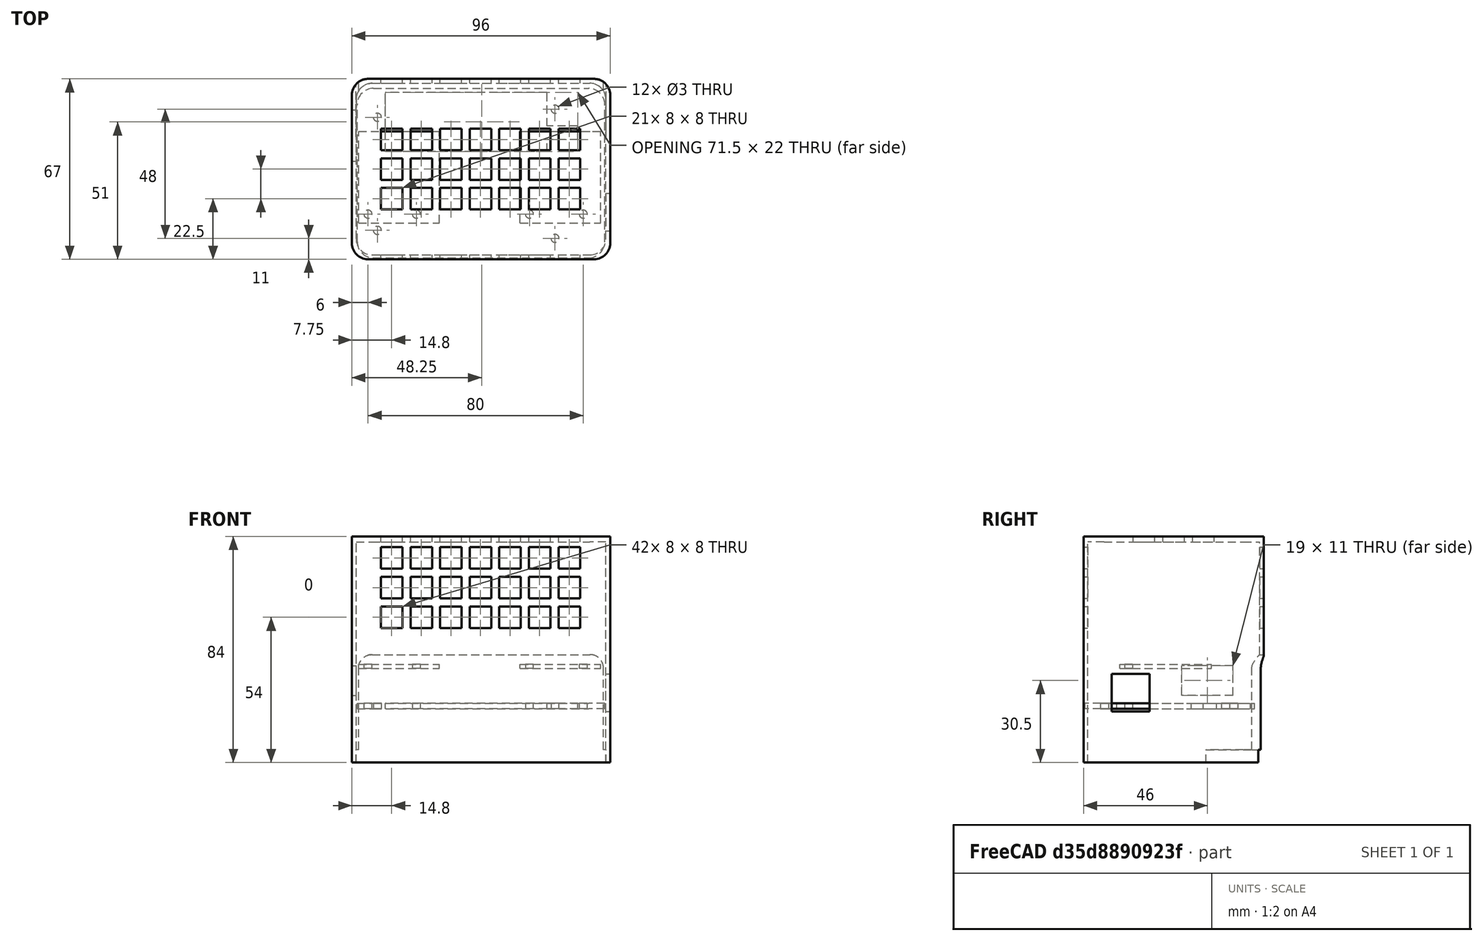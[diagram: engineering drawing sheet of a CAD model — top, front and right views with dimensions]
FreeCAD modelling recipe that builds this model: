
FCSTD DOCUMENT  (FreeCAD 0.18.4R)
Label: BBBCase1
License: CC-BY 3.0
LicenseURL: http://creativecommons.org/licenses/by/3.0/
objects: Part::Box×58, Part::Cylinder×20, Part::MultiFuse×17, Part::Cut×15, Part::Fillet×6, Part::Feature×2, Mesh::Feature×1
note: 118 computed .brp shape members not serialized (recipe doc carries the construction recipe); baked Part::Feature solids carry a one-line shape summary decoded from their .brp

FEATURE [Part::Cylinder] Cylinder
  Angle = 360
  AttacherType = Attacher::AttachEngine3D
  Height = 20
  Placement = pos=(5.5,9.25,0) rot=(0,0,1;0rad)
  Radius = 1.5
FEATURE [Part::Cylinder] Cylinder001
  Angle = 360
  AttacherType = Attacher::AttachEngine3D
  Height = 20
  Placement = pos=(5.5,51.25,0) rot=(0,0,1;0rad)
  Radius = 1.5
FEATURE [Part::Cylinder] Cylinder002
  Angle = 360
  AttacherType = Attacher::AttachEngine3D
  Height = 20
  Placement = pos=(71.5,54.25,0) rot=(0,0,1;0rad)
  Radius = 1.5
FEATURE [Part::Cylinder] Cylinder003
  Angle = 360
  AttacherType = Attacher::AttachEngine3D
  Height = 20
  Placement = pos=(71.5,6.25,0) rot=(0,0,1;0rad)
  Radius = 1.5
FEATURE [Part::Box] Box001  label="base-cube001"
  AttacherType = Attacher::AttachEngine3D
  Height = 2
  Length = 92
  Placement = pos=(-2,-1,0) rot=(0,0,1;0rad)
  Width = 63
FEATURE [Part::Fillet] Fillet
  Base = -> Box001
  Edges = 4 edges r=6: [Edge1,Edge3,Edge5,Edge7]
FEATURE [Part::Cylinder] Cylinder004
  Angle = 360
  AttacherType = Attacher::AttachEngine3D
  Height = 20
  Placement = pos=(5.5,9.25,0) rot=(0,0,1;0rad)
  Radius = 3
FEATURE [Part::Cylinder] Cylinder005
  Angle = 360
  AttacherType = Attacher::AttachEngine3D
  Height = 20
  Placement = pos=(5.5,51.25,0) rot=(0,0,1;0rad)
  Radius = 3
FEATURE [Part::Cylinder] Cylinder006
  Angle = 360
  AttacherType = Attacher::AttachEngine3D
  Height = 20
  Placement = pos=(71.5,54.25,0) rot=(0,0,1;0rad)
  Radius = 3
FEATURE [Part::Cylinder] Cylinder007
  Angle = 360
  AttacherType = Attacher::AttachEngine3D
  Height = 20
  Placement = pos=(71.5,6.25,0) rot=(0,0,1;0rad)
  Radius = 3
FEATURE [Part::MultiFuse] Fusion
  Shapes = -> [Cylinder007,Cylinder006,Cylinder005,Cylinder004,Fillet]
FEATURE [Part::MultiFuse] Fusion001
  Shapes = -> [Cylinder003,Cylinder002,Cylinder001,Cylinder]
FEATURE [Part::Cut] Cut
  Base = -> Fusion
  Tool = -> Fusion001
FEATURE [Part::Box] Box002  label="Cube"
  AttacherType = Attacher::AttachEngine3D
  Height = 10
  Length = 56.5
  Placement = pos=(11,1,0) rot=(0,0,1;0rad)
  Width = 59
FEATURE [Part::Cut] Cut001
  Base = -> Cut
  Tool = -> Box002
FEATURE [Part::Box] Box003  label="base-cube002"
  AttacherType = Attacher::AttachEngine3D
  Height = 2
  Length = 92
  Placement = pos=(-2,-1,0) rot=(0,0,1;0rad)
  Width = 63
FEATURE [Part::Fillet] Fillet001
  Base = -> Box003
  Edges = 4 edges r=6: [Edge1,Edge3,Edge5,Edge7]
  Placement = pos=(0,0,26) rot=(0,0,1;0rad)
FEATURE [Part::Cylinder] Cylinder008
  Angle = 360
  AttacherType = Attacher::AttachEngine3D
  Height = 20
  Placement = pos=(71.5,6.25,20) rot=(0,0,1;0rad)
  Radius = 1.5
FEATURE [Part::Cylinder] Cylinder009
  Angle = 360
  AttacherType = Attacher::AttachEngine3D
  Height = 20
  Placement = pos=(5.5,9.25,20) rot=(0,0,1;0rad)
  Radius = 1.5
FEATURE [Part::Cylinder] Cylinder010
  Angle = 360
  AttacherType = Attacher::AttachEngine3D
  Height = 20
  Placement = pos=(5.5,51.25,20) rot=(0,0,1;0rad)
  Radius = 1.5
FEATURE [Part::Cylinder] Cylinder011
  Angle = 360
  AttacherType = Attacher::AttachEngine3D
  Height = 20
  Placement = pos=(71.5,54.25,20) rot=(0,0,1;0rad)
  Radius = 1.5
FEATURE [Part::MultiFuse] Fusion002
  Shapes = -> [Cylinder008,Cylinder009,Cylinder010,Cylinder011]
FEATURE [Part::Cut] Cut002
  Base = -> Fillet001
  Tool = -> Fusion002
FEATURE [Part::Box] Box005  label="Cube002"
  AttacherType = Attacher::AttachEngine3D
  Height = 1.5
  Length = 30
  Placement = pos=(58.5,12,35) rot=(0,0,1;0rad)
  Width = 34
FEATURE [Part::Cylinder] Cylinder012
  Angle = 360
  AttacherType = Attacher::AttachEngine3D
  Height = 20
  Placement = pos=(2,15.25,20) rot=(0,0,1;0rad)
  Radius = 1.5
FEATURE [Part::Cylinder] Cylinder013
  Angle = 360
  AttacherType = Attacher::AttachEngine3D
  Height = 20
  Placement = pos=(20,15.25,20) rot=(0,0,1;0rad)
  Radius = 1.5
FEATURE [Part::Cylinder] Cylinder014
  Angle = 360
  AttacherType = Attacher::AttachEngine3D
  Height = 20
  Placement = pos=(82,15.25,20) rot=(0,0,1;0rad)
  Radius = 1.5
FEATURE [Part::Cylinder] Cylinder015
  Angle = 360
  AttacherType = Attacher::AttachEngine3D
  Height = 20
  Placement = pos=(62,15.25,20) rot=(0,0,1;0rad)
  Radius = 1.5
FEATURE [Part::Box] Box006  label="Cube003"
  AttacherType = Attacher::AttachEngine3D
  Height = 1.5
  Length = 30
  Placement = pos=(-1.5,12,35) rot=(0,0,1;0rad)
  Width = 34
FEATURE [Part::MultiFuse] Fusion003
  Shapes = -> [Cylinder015,Cylinder014,Cylinder013,Cylinder012]
FEATURE [Part::Cut] Cut003  label="PRE-GPS-BASE"
  Base = -> Cut002
  Tool = -> Fusion003
FEATURE [Part::Cylinder] Cylinder016
  Angle = 360
  AttacherType = Attacher::AttachEngine3D
  Height = 20
  Placement = pos=(2,15.25,20) rot=(0,0,1;0rad)
  Radius = 1.5
FEATURE [Part::Cylinder] Cylinder017
  Angle = 360
  AttacherType = Attacher::AttachEngine3D
  Height = 20
  Placement = pos=(20,15.25,20) rot=(0,0,1;0rad)
  Radius = 1.5
FEATURE [Part::Cylinder] Cylinder018
  Angle = 360
  AttacherType = Attacher::AttachEngine3D
  Height = 20
  Placement = pos=(82,15.25,20) rot=(0,0,1;0rad)
  Radius = 1.5
FEATURE [Part::Cylinder] Cylinder019
  Angle = 360
  AttacherType = Attacher::AttachEngine3D
  Height = 20
  Placement = pos=(62,15.25,20) rot=(0,0,1;0rad)
  Radius = 1.5
FEATURE [Part::MultiFuse] Fusion004
  Shapes = -> [Cylinder017,Cylinder016]
FEATURE [Part::MultiFuse] Fusion005
  Shapes = -> [Cylinder019,Cylinder018]
FEATURE [Part::Cut] Cut004  label="SUP-GPS-B"
  Base = -> Box006
  Tool = -> Fusion004
FEATURE [Part::Cut] Cut005  label="SUP-GPS-A"
  Base = -> Box005
  Tool = -> Fusion005
FEATURE [Part::Box] Box007  label="Cube004"
  AttacherType = Attacher::AttachEngine3D
  Height = 10
  Length = 87
  Placement = pos=(0.5,20,0) rot=(0,0,1;0rad)
  Width = 20
FEATURE [Part::Cut] Cut006  label="BOTTON-BASE"
  Base = -> Cut001
  Tool = -> Box007
FEATURE [Part::Box] Box008  label="Cube005"
  AttacherType = Attacher::AttachEngine3D
  Height = 10
  Length = 60
  Placement = pos=(8.5,38.5,20) rot=(0,0,1;0rad)
  Width = 22
FEATURE [Part::Cut] Cut007  label="pre-MIDDLE-BASE"
  Base = -> Cut003
  Tool = -> Box008
FEATURE [Part::Box] Box009  label="Cube006"
  AttacherType = Attacher::AttachEngine3D
  Height = 10
  Length = 12
  Placement = pos=(68,43,20) rot=(0,0,1;0rad)
  Width = 5
FEATURE [Part::Cut] Cut008  label="MIDDLE-BASE"
  Base = -> Cut007
  Placement = pos=(0,0,-6) rot=(0,0,1;0rad)
  Tool = -> Box009
FEATURE [Mesh::Feature] lcd_housing
  Placement = pos=(-1,62,-0.01) rot=(0,0,1;0rad)
FEATURE [Part::Box] Box010  label="base-cube003"
  AttacherType = Attacher::AttachEngine3D
  Height = 4.5
  Length = 92
  Placement = pos=(-2,47,0) rot=(0,0,1;0rad)
  Width = 52
FEATURE [Part::Fillet] Fillet002
  Base = -> Box010
  Edges = 2 edges r=5: [Edge3,Edge7]
FEATURE [Part::Feature] lcd_housing001
  shape: bbox 90 x 37 x 39.75 mm, 3808 faces, 0 solids (baked)
FEATURE [Part::Feature] lcd_housing001_solid  label="lcd_housing001 (Solid)"
  shape: bbox 90 x 37 x 39.75 mm, 3808 faces (baked)
FEATURE [Part::MultiFuse] Fusion006
  Shapes = -> [lcd_housing001_solid,Fillet002,Cut006]
FEATURE [Part::Box] Box011  label="Cube007"
  AttacherType = Attacher::AttachEngine3D
  Height = 10
  Length = 82
  Placement = pos=(3,59,-1) rot=(0,0,1;0rad)
  Width = 36
FEATURE [Part::Cut] Cut009  label="bottom-base"
  Base = -> Fusion006
  Tool = -> Box011
FEATURE [Part::Box] Box012  label="base-cube004"
  AttacherType = Attacher::AttachEngine3D
  Height = 82
  Length = 92.8
  Placement = pos=(-2,-1,0) rot=(0,0,1;0rad)
  Width = 63.8
FEATURE [Part::Fillet] Fillet003
  Base = -> Box012
  Edges = 4 edges r=6: [Edge1,Edge3,Edge5,Edge7]
  Placement = pos=(1.6,1.6,26) rot=(0,0,1;0rad)
FEATURE [Part::Box] Box013  label="base-cube005"
  AttacherType = Attacher::AttachEngine3D
  Height = 84
  Length = 96
  Placement = pos=(-2,-1,0) rot=(0,0,1;0rad)
  Width = 67
FEATURE [Part::Fillet] Fillet004
  Base = -> Box013
  Edges = 4 edges r=6: [Edge1,Edge3,Edge5,Edge7]
  Placement = pos=(0,0,26) rot=(0,0,1;0rad)
FEATURE [Part::Cut] Cut009002001002
  Base = -> Fillet004
  Placement = pos=(-2,-0.5,-26) rot=(0,0,1;0rad)
  Tool = -> Fillet003
FEATURE [Part::Box] Box  label="Cube008"
  AttacherType = Attacher::AttachEngine3D
  Height = 35.5
  Length = 91
  Placement = pos=(-1.5,53,4.6) rot=(0,0,1;0rad)
  Width = 10
FEATURE [Part::Fillet] Fillet005
  Base = -> Box
  Edges = 2 edges r=5: [Edge2,Edge6]
  Placement = pos=(0,5,0) rot=(0,0,1;0rad)
FEATURE [Part::Box] Box014  label="Cube009"
  AttacherType = Attacher::AttachEngine3D
  Height = 4.8
  Length = 93
  Placement = pos=(-2.5,44,0) rot=(0,0,1;0rad)
  Width = 64
FEATURE [Part::MultiFuse] Fusion007
  Shapes = -> [Box014,Fillet005]
FEATURE [Part::Cut] Cut009002001003
  Base = -> Cut009002001002
  Tool = -> Fusion007
FEATURE [Part::Box] Box015  label="Cube010"
  AttacherType = Attacher::AttachEngine3D
  Height = 8
  Length = 8
  Placement = pos=(5,-9,72) rot=(0,0,1;0rad)
  Width = 89
FEATURE [Part::Box] Box016  label="Cube011"
  AttacherType = Attacher::AttachEngine3D
  Height = 8
  Length = 8
  Placement = pos=(16,-9,72) rot=(0,0,1;0rad)
  Width = 89
FEATURE [Part::Box] Box017  label="Cube012"
  AttacherType = Attacher::AttachEngine3D
  Height = 8
  Length = 8
  Placement = pos=(27,-9,72) rot=(0,0,1;0rad)
  Width = 89
FEATURE [Part::Box] Box018  label="Cube013"
  AttacherType = Attacher::AttachEngine3D
  Height = 8
  Length = 8
  Placement = pos=(38,-9,72) rot=(0,0,1;0rad)
  Width = 89
FEATURE [Part::Box] Box019  label="Cube014"
  AttacherType = Attacher::AttachEngine3D
  Height = 8
  Length = 8
  Placement = pos=(49,-9,72) rot=(0,0,1;0rad)
  Width = 89
FEATURE [Part::Box] Box020  label="Cube015"
  AttacherType = Attacher::AttachEngine3D
  Height = 8
  Length = 8
  Placement = pos=(60,-9,72) rot=(0,0,1;0rad)
  Width = 89
FEATURE [Part::Box] Box021  label="Cube016"
  AttacherType = Attacher::AttachEngine3D
  Height = 8
  Length = 8
  Placement = pos=(71,-9,72) rot=(0,0,1;0rad)
  Width = 89
FEATURE [Part::MultiFuse] Fusion008
  Placement = pos=(1.8,0,0) rot=(0,0,1;0rad)
  Shapes = -> [Box021,Box015,Box016,Box017,Box018,Box019,Box020]
FEATURE [Part::Box] Box022  label="Cube017"
  AttacherType = Attacher::AttachEngine3D
  Height = 8
  Length = 8
  Placement = pos=(5,-9,72) rot=(0,0,1;0rad)
  Width = 89
FEATURE [Part::Box] Box023  label="Cube018"
  AttacherType = Attacher::AttachEngine3D
  Height = 8
  Length = 8
  Placement = pos=(16,-9,72) rot=(0,0,1;0rad)
  Width = 89
FEATURE [Part::Box] Box024  label="Cube019"
  AttacherType = Attacher::AttachEngine3D
  Height = 8
  Length = 8
  Placement = pos=(27,-9,72) rot=(0,0,1;0rad)
  Width = 89
FEATURE [Part::Box] Box025  label="Cube020"
  AttacherType = Attacher::AttachEngine3D
  Height = 8
  Length = 8
  Placement = pos=(38,-9,72) rot=(0,0,1;0rad)
  Width = 89
FEATURE [Part::Box] Box026  label="Cube021"
  AttacherType = Attacher::AttachEngine3D
  Height = 8
  Length = 8
  Placement = pos=(49,-9,72) rot=(0,0,1;0rad)
  Width = 89
FEATURE [Part::Box] Box027  label="Cube022"
  AttacherType = Attacher::AttachEngine3D
  Height = 8
  Length = 8
  Placement = pos=(60,-9,72) rot=(0,0,1;0rad)
  Width = 89
FEATURE [Part::Box] Box028  label="Cube023"
  AttacherType = Attacher::AttachEngine3D
  Height = 8
  Length = 8
  Placement = pos=(71,-9,72) rot=(0,0,1;0rad)
  Width = 89
FEATURE [Part::MultiFuse] Fusion009
  Placement = pos=(1.8,0,-11) rot=(0,0,1;0rad)
  Shapes = -> [Box028,Box022,Box023,Box024,Box025,Box026,Box027]
FEATURE [Part::Box] Box029  label="Cube024"
  AttacherType = Attacher::AttachEngine3D
  Height = 8
  Length = 8
  Placement = pos=(5,-9,72) rot=(0,0,1;0rad)
  Width = 89
FEATURE [Part::Box] Box030  label="Cube025"
  AttacherType = Attacher::AttachEngine3D
  Height = 8
  Length = 8
  Placement = pos=(16,-9,72) rot=(0,0,1;0rad)
  Width = 89
FEATURE [Part::Box] Box031  label="Cube026"
  AttacherType = Attacher::AttachEngine3D
  Height = 8
  Length = 8
  Placement = pos=(27,-9,72) rot=(0,0,1;0rad)
  Width = 89
FEATURE [Part::Box] Box032  label="Cube027"
  AttacherType = Attacher::AttachEngine3D
  Height = 8
  Length = 8
  Placement = pos=(38,-9,72) rot=(0,0,1;0rad)
  Width = 89
FEATURE [Part::Box] Box033  label="Cube028"
  AttacherType = Attacher::AttachEngine3D
  Height = 8
  Length = 8
  Placement = pos=(49,-9,72) rot=(0,0,1;0rad)
  Width = 89
FEATURE [Part::Box] Box034  label="Cube029"
  AttacherType = Attacher::AttachEngine3D
  Height = 8
  Length = 8
  Placement = pos=(60,-9,72) rot=(0,0,1;0rad)
  Width = 89
FEATURE [Part::Box] Box035  label="Cube030"
  AttacherType = Attacher::AttachEngine3D
  Height = 8
  Length = 8
  Placement = pos=(71,-9,72) rot=(0,0,1;0rad)
  Width = 89
FEATURE [Part::MultiFuse] Fusion010
  Placement = pos=(1.8,0,-22) rot=(0,0,1;0rad)
  Shapes = -> [Box035,Box029,Box030,Box031,Box032,Box033,Box034]
FEATURE [Part::MultiFuse] Fusion011
  Shapes = -> [Fusion010,Fusion008,Fusion009]
FEATURE [Part::Box] Box036  label="Cube031"
  AttacherType = Attacher::AttachEngine3D
  Height = 8
  Length = 8
  Placement = pos=(5,-9,72) rot=(0,0,1;0rad)
  Width = 89
FEATURE [Part::Box] Box037  label="Cube032"
  AttacherType = Attacher::AttachEngine3D
  Height = 8
  Length = 8
  Placement = pos=(16,-9,72) rot=(0,0,1;0rad)
  Width = 89
FEATURE [Part::Box] Box038  label="Cube033"
  AttacherType = Attacher::AttachEngine3D
  Height = 8
  Length = 8
  Placement = pos=(27,-9,72) rot=(0,0,1;0rad)
  Width = 89
FEATURE [Part::Box] Box039  label="Cube034"
  AttacherType = Attacher::AttachEngine3D
  Height = 8
  Length = 8
  Placement = pos=(38,-9,72) rot=(0,0,1;0rad)
  Width = 89
FEATURE [Part::Box] Box040  label="Cube035"
  AttacherType = Attacher::AttachEngine3D
  Height = 8
  Length = 8
  Placement = pos=(49,-9,72) rot=(0,0,1;0rad)
  Width = 89
FEATURE [Part::Box] Box041  label="Cube036"
  AttacherType = Attacher::AttachEngine3D
  Height = 8
  Length = 8
  Placement = pos=(60,-9,72) rot=(0,0,1;0rad)
  Width = 89
FEATURE [Part::Box] Box042  label="Cube037"
  AttacherType = Attacher::AttachEngine3D
  Height = 8
  Length = 8
  Placement = pos=(71,-9,72) rot=(0,0,1;0rad)
  Width = 89
FEATURE [Part::Box] Box043  label="Cube038"
  AttacherType = Attacher::AttachEngine3D
  Height = 8
  Length = 8
  Placement = pos=(5,-9,72) rot=(0,0,1;0rad)
  Width = 89
FEATURE [Part::Box] Box044  label="Cube039"
  AttacherType = Attacher::AttachEngine3D
  Height = 8
  Length = 8
  Placement = pos=(16,-9,72) rot=(0,0,1;0rad)
  Width = 89
FEATURE [Part::Box] Box045  label="Cube040"
  AttacherType = Attacher::AttachEngine3D
  Height = 8
  Length = 8
  Placement = pos=(27,-9,72) rot=(0,0,1;0rad)
  Width = 89
FEATURE [Part::Box] Box046  label="Cube041"
  AttacherType = Attacher::AttachEngine3D
  Height = 8
  Length = 8
  Placement = pos=(38,-9,72) rot=(0,0,1;0rad)
  Width = 89
FEATURE [Part::Box] Box047  label="Cube042"
  AttacherType = Attacher::AttachEngine3D
  Height = 8
  Length = 8
  Placement = pos=(49,-9,72) rot=(0,0,1;0rad)
  Width = 89
FEATURE [Part::Box] Box048  label="Cube043"
  AttacherType = Attacher::AttachEngine3D
  Height = 8
  Length = 8
  Placement = pos=(60,-9,72) rot=(0,0,1;0rad)
  Width = 89
FEATURE [Part::Box] Box049  label="Cube044"
  AttacherType = Attacher::AttachEngine3D
  Height = 8
  Length = 8
  Placement = pos=(71,-9,72) rot=(0,0,1;0rad)
  Width = 89
FEATURE [Part::Box] Box050  label="Cube045"
  AttacherType = Attacher::AttachEngine3D
  Height = 8
  Length = 8
  Placement = pos=(5,-9,72) rot=(0,0,1;0rad)
  Width = 89
FEATURE [Part::Box] Box051  label="Cube046"
  AttacherType = Attacher::AttachEngine3D
  Height = 8
  Length = 8
  Placement = pos=(16,-9,72) rot=(0,0,1;0rad)
  Width = 89
FEATURE [Part::Box] Box052  label="Cube047"
  AttacherType = Attacher::AttachEngine3D
  Height = 8
  Length = 8
  Placement = pos=(27,-9,72) rot=(0,0,1;0rad)
  Width = 89
FEATURE [Part::Box] Box053  label="Cube048"
  AttacherType = Attacher::AttachEngine3D
  Height = 8
  Length = 8
  Placement = pos=(38,-9,72) rot=(0,0,1;0rad)
  Width = 89
FEATURE [Part::Box] Box054  label="Cube049"
  AttacherType = Attacher::AttachEngine3D
  Height = 8
  Length = 8
  Placement = pos=(49,-9,72) rot=(0,0,1;0rad)
  Width = 89
FEATURE [Part::Box] Box055  label="Cube050"
  AttacherType = Attacher::AttachEngine3D
  Height = 8
  Length = 8
  Placement = pos=(60,-9,72) rot=(0,0,1;0rad)
  Width = 89
FEATURE [Part::Box] Box056  label="Cube051"
  AttacherType = Attacher::AttachEngine3D
  Height = 8
  Length = 8
  Placement = pos=(71,-9,72) rot=(0,0,1;0rad)
  Width = 89
FEATURE [Part::MultiFuse] Fusion012
  Placement = pos=(1.8,0,0) rot=(0,0,1;0rad)
  Shapes = -> [Box042,Box036,Box037,Box038,Box039,Box040,Box041]
FEATURE [Part::MultiFuse] Fusion013
  Placement = pos=(1.8,0,-11) rot=(0,0,1;0rad)
  Shapes = -> [Box049,Box043,Box044,Box045,Box046,Box047,Box048]
FEATURE [Part::MultiFuse] Fusion014
  Placement = pos=(1.8,0,-22) rot=(0,0,1;0rad)
  Shapes = -> [Box056,Box050,Box051,Box052,Box053,Box054,Box055]
FEATURE [Part::MultiFuse] Fusion015
  Placement = pos=(0,97,20) rot=(1,0,0;1.5708rad)
  Shapes = -> [Fusion014,Fusion012,Fusion013]
FEATURE [Part::MultiFuse] Fusion016
  Shapes = -> [Fusion011,Fusion015]
FEATURE [Part::Cut] Cut009002001004  label="pre-outside-cape"
  Base = -> Cut009002001003
  Tool = -> Fusion016
FEATURE [Part::Box] Box057  label="Cube052"
  AttacherType = Attacher::AttachEngine3D
  Height = 14
  Length = 14
  Placement = pos=(82,9,19) rot=(0,0,1;0rad)
  Width = 14
FEATURE [Part::Cut] Cut009002001005
  Base = -> Cut009002001004
  Tool = -> Box057
FEATURE [Part::Box] Box058  label="Cube053"
  AttacherType = Attacher::AttachEngine3D
  Height = 11
  Length = 14
  Placement = pos=(-7,35,25) rot=(0,0,1;0rad)
  Width = 19
FEATURE [Part::Cut] Cut009002001006  label="outside-frame"
  Base = -> Cut009002001005
  Tool = -> Box058
